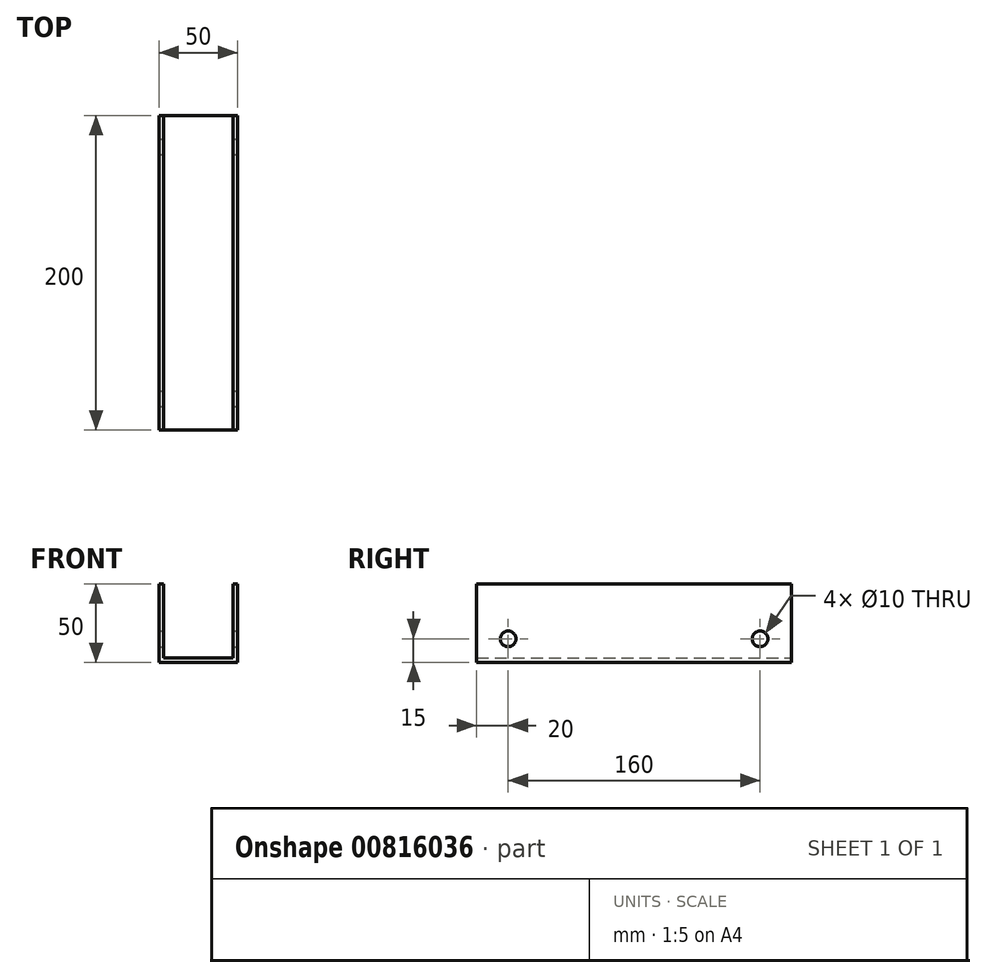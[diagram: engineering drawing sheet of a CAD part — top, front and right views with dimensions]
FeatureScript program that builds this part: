
annotation { "Feature Type Name" : "Feature", "Feature Type Description" : "" }
export const myFeature = defineFeature(function(context is Context, id is Id, definition is map)
    precondition{}
    {
        {
            var Q0;
            Q0=qCreatedBy(makeId("Front.planeOp"),FACE);
            var sketch = newSketch(context, id + "F0", { "sketchPlane" : qUnion([Q0])});
            skLineSegment(sketch, "E0.bottom", {"start": v(0, 0) * mm, "end": v(50, 0) * mm});
            skLineSegment(sketch, "E0.top", {"start": v(0, 50) * mm, "end": v(50, 50) * mm});
            skLineSegment(sketch, "E0.left", {"start": v(0, 0) * mm, "end": v(0, 50) * mm});
            skLineSegment(sketch, "E0.right", {"start": v(50, 0) * mm, "end": v(50, 50) * mm});
            skLineSegment(sketch, "E1.bottom", {"start": v(3, 50) * mm, "end": v(47, 50) * mm});
            skLineSegment(sketch, "E1.top", {"start": v(3, 3) * mm, "end": v(47, 3) * mm});
            skLineSegment(sketch, "E1.left", {"start": v(3, 50) * mm, "end": v(3, 3) * mm});
            skLineSegment(sketch, "E1.right", {"start": v(47, 50) * mm, "end": v(47, 3) * mm});
            skPoint(sketch, "E2", {"position": v(25, 50) * mm});
            skSolve(sketch);
        }
        {
            var Q0;
            Q0=makeQuery(id+"F0.imprint","IMPRINT",FACE,{"disambiguationData":[TD([[makeQuery(id+"F0.imprint","IMPRINT",EDGE,{"derivedFrom":sQuery(id+"F0.wireOp",EDGE,"E0.bottom")}),1.0]])]});
            extrude(context, id + "F1", {"entities" : qUnion([Q0]), "depth" : 200 * mm, "offsetDistance" : 25 * mm});
        }
        {
            var Q0;
            Q0=makeQuery(id+"F1.opExtrude","SWEPT_FACE",FACE,{"disambiguationData":[OSD([sQuery(id+"F0.wireOp",EDGE,"E0.right")])]});
            var sketch = newSketch(context, id + "F2", { "sketchPlane" : qUnion([Q0])});
            skPoint(sketch, "E3", {"position": v(-180, 15) * mm});
            skPoint(sketch, "E4", {"position": v(-20, 15) * mm});
            skSolve(sketch);
        }
        {
            var Q0;
            Q0=sQuery(id+"F2.wireOp",VERTEX,"E3");
            var Q1;
            Q1=sQuery(id+"F2.wireOp",VERTEX,"E4");
            var Q2;
            Q2=makeQuery(id+"F1.opExtrude","SWEPT_BODY",BODY,{"disambiguationData":[OSD([sQuery(id+"F0.wireOp",EDGE,"E0.bottom"),sQuery(id+"F0.wireOp",EDGE,"E0.top"),sQuery(id+"F0.wireOp",EDGE,"E0.left"),sQuery(id+"F0.wireOp",EDGE,"E0.right"),sQuery(id+"F0.wireOp",EDGE,"E1.top"),sQuery(id+"F0.wireOp",EDGE,"E1.left"),sQuery(id+"F0.wireOp",EDGE,"E1.right")])]});
            hole(context, id + "F3", {"style" : HoleStyle.SIMPLE, "endStyle" : HoleEndStyle.BLIND, "holeDiameter" : 10 * mm, "majorDiameter" : 5 * mm, "holeDepth" : 50 * mm, "isTappedThrough" : true, "tappedDepth" : 12 * mm, "tapClearance" : 3, "startFromSketch" : true, "locations" : qUnion([Q0, Q1]), "scope" : qUnion([Q2])});
        }
    });
